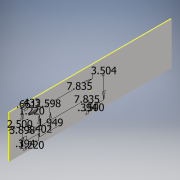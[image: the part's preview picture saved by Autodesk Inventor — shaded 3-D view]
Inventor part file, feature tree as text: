
AUTODESK INVENTOR PART (.ipt)
format: ipt  version: 2017 (Build 210142000, 142)  size: 124,928 bytes
history: native  units: in
note: dims shown in document units (in); Inventor stores cm internally (conversion verified against a paired STEP export)
features: sketch x2, extrude x1, other x1, hole x1
ambient origin geometry x8: Origin, YZ Plane, XZ Plane, XY Plane, X Axis, Y Axis, Z Axis, Center Point
bodies: Solid1 (feature_tree)
feature tree (5):
  extrude  "pdu nmt right side panel"  Depth=5.22in
  other  "snap psu"
  hole  "snap psu holes"  [1 undecoded]
  sketch  "Sketch1"  dims[d0=20.0in d1=5.22in]
  sketch  "Sketch5"  dims[d2=0.125in d3=0.0in d19=0.394in d20=1.22in d21=3.898in d22=0.5in d23=0.433in d24=0.661in d25=2.5in d26=0.134in d27=0.75in d28=0.248in d29=0.25in d30=90.0deg d31=1.0in d32=0.8108in d33=0.394in d34=3.504in d35=1.22in d36=2.402in d37=2.598in d38=1.949in d39=7.835in d40=7.835in]
note: 1 required parameter value undecoded (feature->parameter linkage not recoverable at this tier; creation-order binding heuristic only, values carry confidence <= 0.55)
